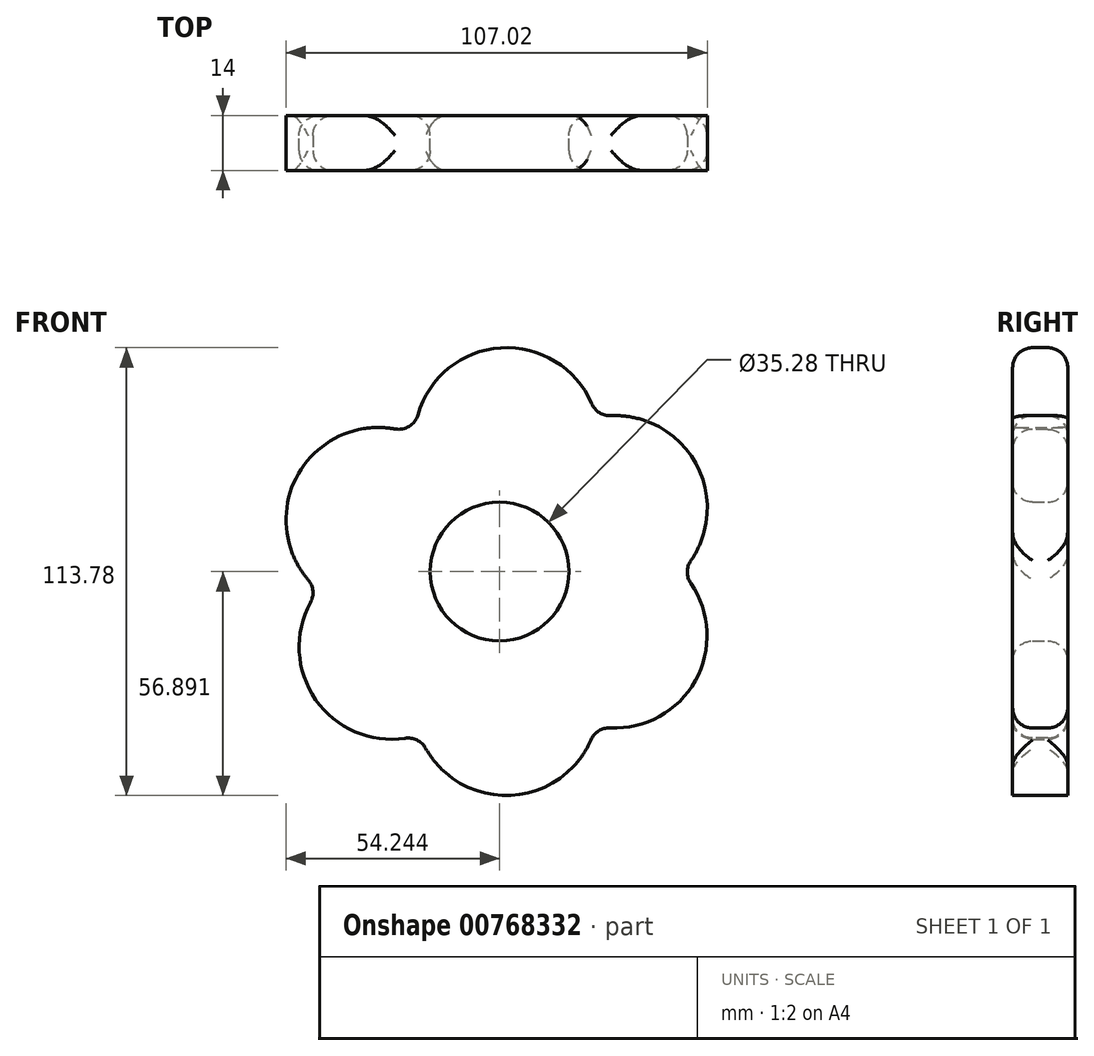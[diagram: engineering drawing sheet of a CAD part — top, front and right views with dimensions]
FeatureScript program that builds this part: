
annotation { "Feature Type Name" : "Feature", "Feature Type Description" : "" }
export const myFeature = defineFeature(function(context is Context, id is Id, definition is map)
    precondition{}
    {
        {
            var Q0;
            Q0=qCreatedBy(makeId("Front.planeOp"),FACE);
            var sketch = newSketch(context, id + "F0", { "sketchPlane" : qUnion([Q0])});
            skArc(sketch, "E0", {"start": v(-28.58, -11.4) * mm, "mid": v(-25.12, -5.23) * mm, "end": v(-23.67, 1.7) * mm});
            skArc(sketch, "E1.1.0", {"start": v(-62.29, -14.87) * mm, "mid": v(-63.02, -42.7) * mm, "end": v(-36.66, -51.64) * mm});
            skArc(sketch, "E1.2.0", {"start": v(-36.66, -51.64) * mm, "mid": v(-13.45, -67) * mm, "end": v(8.1, -49.4) * mm});
            skArc(sketch, "E1.3.0", {"start": v(8.1, -49.4) * mm, "mid": v(33.43, -37.85) * mm, "end": v(29.92, -10.24) * mm});
            skArc(sketch, "E1.4.0", {"start": v(29.92, -10.24) * mm, "mid": v(33.55, 17.36) * mm, "end": v(8.27, 29) * mm});
            skArc(sketch, "E1.5.0", {"start": v(8.27, 29) * mm, "mid": v(-16.7, 46.64) * mm, "end": v(-37.9, 24.6) * mm});
            skPoint(sketch, "E1.center", {"position": v(-16.3, -10.14) * mm});
            skLineSegment(sketch, "E1.anchor1", {"start": v(-16.3, -10.14) * mm, "end": v(-47.1, 3) * mm, "construction": true});
            skLineSegment(sketch, "E1.anchor2", {"start": v(-16.3, -10.14) * mm, "end": v(-14.48, 23.29) * mm, "construction": true});
            skArc(sketch, "E2.trimOffspring", {"start": v(-21.74, -21.21) * mm, "mid": v(-24.52, -15.86) * mm, "end": v(-28.58, -11.4) * mm});
            skArc(sketch, "E3.trimOffspring", {"start": v(-9.8, -20.61) * mm, "mid": v(-15.8, -20.14) * mm, "end": v(-21.74, -21.21) * mm});
            skArc(sketch, "E4.trimOffspring", {"start": v(-3.97, -10.17) * mm, "mid": v(-7.56, -15.01) * mm, "end": v(-9.8, -20.61) * mm});
            skArc(sketch, "E5.trimOffspring", {"start": v(-9.75, 0.3) * mm, "mid": v(-7.54, -5.3) * mm, "end": v(-3.97, -10.17) * mm});
            skArc(sketch, "E6.trimOffspring", {"start": v(-37.9, 24.6) * mm, "mid": v(-67.05, 15.34) * mm, "end": v(-62.29, -14.87) * mm});
            skArc(sketch, "E7.trimOffspring", {"start": v(-23.67, 1.7) * mm, "mid": v(-16.81, -0.06) * mm, "end": v(-9.75, 0.3) * mm});
            skCircle(sketch, "E8", {"center": v(-16.3, -10.14) * mm, "radius": 17.64 * mm});
            skSolve(sketch);
        }
        {
            var Q0;
            Q0 = qSketchRegion(id + "F0", true);
            extrude(context, id + "F1", {"entities" : qUnion([Q0]), "depth" : 14 * mm, "offsetDistance" : 25.4 * mm});
        }
        {
            var Q0;
            Q0=makeQuery(id+"F1.opExtrude","SWEPT_FACE",FACE,{"disambiguationData":[OSD([sQuery(id+"F0.wireOp",EDGE,"E1.3.0")])]});
            var Q1;
            Q1=makeQuery(id+"F1.opExtrude","SWEPT_FACE",FACE,{"disambiguationData":[OSD([sQuery(id+"F0.wireOp",EDGE,"E1.5.0")])]});
            var Q2;
            Q2=makeQuery(id+"F1.opExtrude","SWEPT_FACE",FACE,{"disambiguationData":[OSD([sQuery(id+"F0.wireOp",EDGE,"E1.1.0")])]});
            fillet(context, id + "F2", {"entities" : qUnion([Q0, Q1, Q2]), "radius" : 5.08 * mm, "tangentPropagation" : true, "allowEdgeOverflow" : false});
        }
        {
            var Q0;
            Q0=makeQuery(id+"F1.opExtrude","CAP_EDGE",EDGE,{"disambiguationData":[OSD([sQuery(id+"F0.wireOp",EDGE,"E8")])],"isStart":false});
            var Q1;
            Q1=makeQuery(id+"F1.opExtrude","CAP_EDGE",EDGE,{"disambiguationData":[OSD([sQuery(id+"F0.wireOp",EDGE,"E8")])],"isStart":true});
            fillet(context, id + "F3", {"entities" : qUnion([Q0, Q1]), "radius" : 5.08 * mm, "tangentPropagation" : true, "allowEdgeOverflow" : false});
        }
    });
